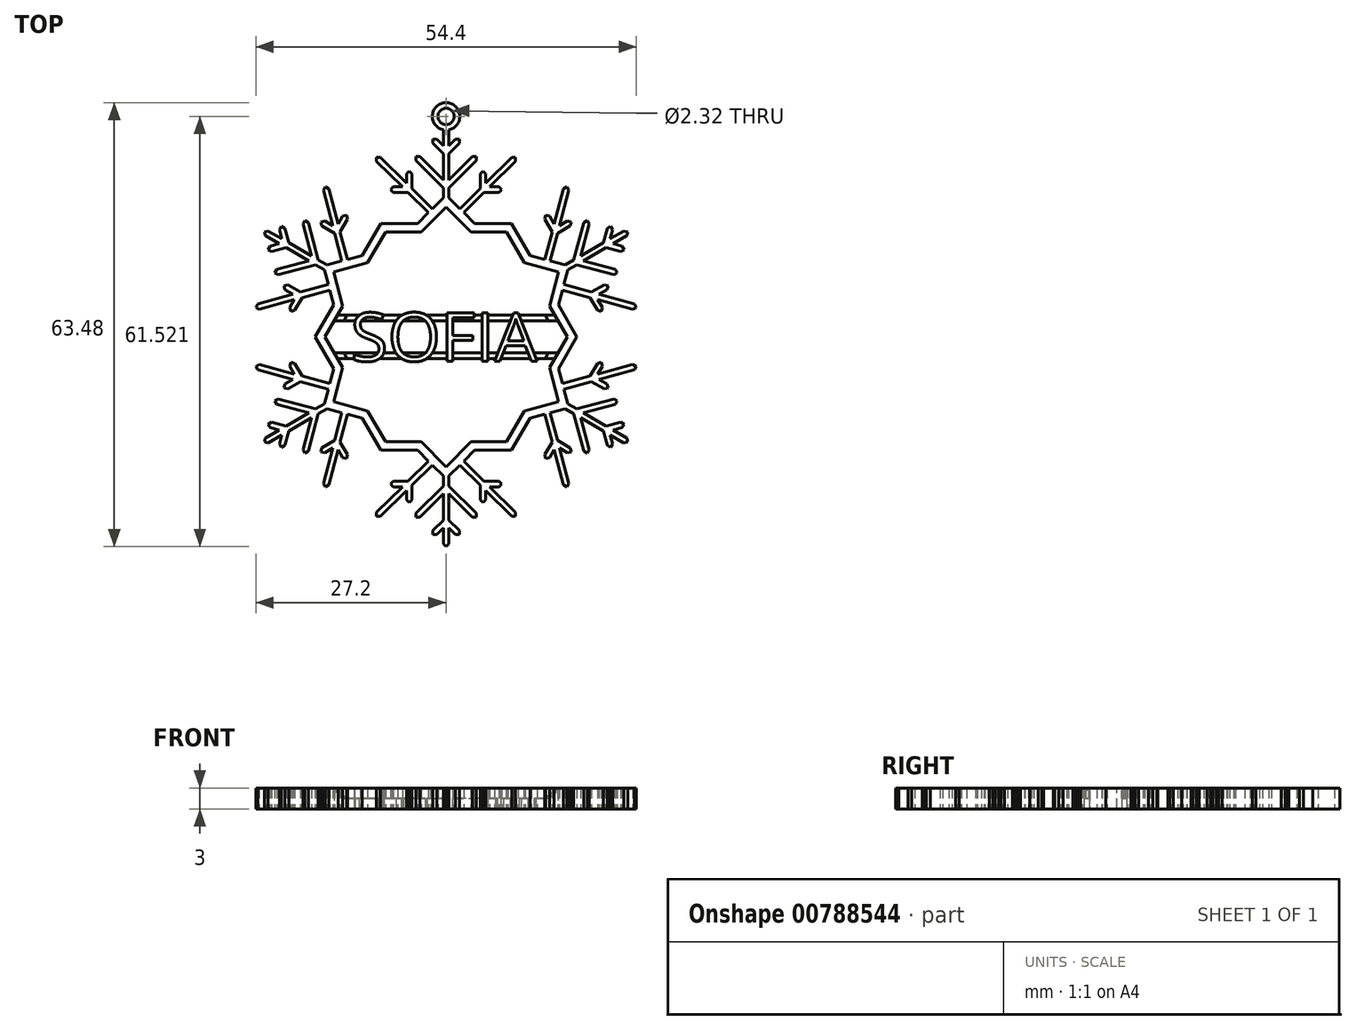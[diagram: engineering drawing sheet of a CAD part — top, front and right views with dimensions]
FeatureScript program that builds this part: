
annotation { "Feature Type Name" : "Feature", "Feature Type Description" : "" }
export const myFeature = defineFeature(function(context is Context, id is Id, definition is map)
    precondition{}
    {
        {
            var Q0;
            Q0=qCreatedBy(makeId("Top.planeOp"),FACE);
            var sketch = newSketch(context, id + "F0", { "sketchPlane" : qUnion([Q0])});
            skLineSegment(sketch, "E0", {"start": v(0, 0) * mm, "end": v(0, 68.59) * mm, "construction": true});
            skLineSegment(sketch, "E1", {"start": v(0, 0) * mm, "end": v(35, 60.61) * mm, "construction": true});
            skLineSegment(sketch, "E2", {"start": v(0, 0) * mm, "end": v(-32.87, 56.93) * mm, "construction": true});
            skLineSegment(sketch, "E3", {"start": v(-8.66, 15) * mm, "end": v(-3.57, 15) * mm});
            skLineSegment(sketch, "E4", {"start": v(-3.57, 15) * mm, "end": v(0, 18.57) * mm});
            skLineSegment(sketch, "E5", {"start": v(-0.4, 19.87) * mm, "end": v(-1.95, 18.32) * mm});
            skLineSegment(sketch, "E6", {"start": v(-4.07, 16.2) * mm, "end": v(-9.35, 16.2) * mm});
            skLineSegment(sketch, "E7", {"start": v(-0.4, 29.6) * mm, "end": v(0, 30) * mm});
            skLineSegment(sketch, "E8", {"start": v(-0.4, 27.32) * mm, "end": v(-1.35, 28.28) * mm});
            skLineSegment(sketch, "E9", {"start": v(-1.35, 28.28) * mm, "end": v(-1.92, 28.28) * mm});
            skLineSegment(sketch, "E10", {"start": v(-1.92, 28.28) * mm, "end": v(-1.92, 27.71) * mm});
            skLineSegment(sketch, "E11", {"start": v(-1.92, 27.71) * mm, "end": v(-0.4, 26.2) * mm});
            skLineSegment(sketch, "E12", {"start": v(-1.95, 18.32) * mm, "end": v(-4.86, 21.2) * mm});
            skLineSegment(sketch, "E13", {"start": v(-9.38, 25.67) * mm, "end": v(-9.94, 25.67) * mm});
            skLineSegment(sketch, "E14", {"start": v(-9.94, 25.67) * mm, "end": v(-9.94, 25.1) * mm});
            skLineSegment(sketch, "E15", {"start": v(-9.94, 25.1) * mm, "end": v(-6.24, 21.43) * mm});
            skLineSegment(sketch, "E16", {"start": v(-5.66, 22) * mm, "end": v(-5.66, 23.3) * mm});
            skLineSegment(sketch, "E17", {"start": v(-5.66, 23.3) * mm, "end": v(-5.27, 23.7) * mm});
            skLineSegment(sketch, "E18", {"start": v(-5.27, 23.7) * mm, "end": v(-4.86, 23.3) * mm});
            skLineSegment(sketch, "E19", {"start": v(-4.86, 23.3) * mm, "end": v(-4.86, 21.2) * mm});
            skLineSegment(sketch, "E20", {"start": v(-5.43, 20.63) * mm, "end": v(-7.54, 20.63) * mm});
            skLineSegment(sketch, "E21", {"start": v(-7.54, 20.63) * mm, "end": v(-7.94, 21.03) * mm});
            skLineSegment(sketch, "E22", {"start": v(-6.24, 21.43) * mm, "end": v(-7.54, 21.43) * mm});
            skLineSegment(sketch, "E23", {"start": v(-7.54, 21.43) * mm, "end": v(-7.94, 21.03) * mm});
            skLineSegment(sketch, "E24.trimOffspring", {"start": v(-2.52, 17.75) * mm, "end": v(-4.07, 16.2) * mm});
            skLineSegment(sketch, "E25", {"start": v(-0.4, 22.44) * mm, "end": v(-3.74, 25.77) * mm});
            skLineSegment(sketch, "E26", {"start": v(-3.74, 25.77) * mm, "end": v(-4.3, 25.77) * mm});
            skLineSegment(sketch, "E27", {"start": v(-4.3, 25.77) * mm, "end": v(-4.3, 25.2) * mm});
            skLineSegment(sketch, "E28", {"start": v(-4.3, 25.2) * mm, "end": v(-0.4, 21.3) * mm});
            skLineSegment(sketch, "E29.trimOffspring", {"start": v(-5.66, 22) * mm, "end": v(-9.38, 25.67) * mm});
            skLineSegment(sketch, "E30.trimOffspring", {"start": v(-5.43, 20.63) * mm, "end": v(-2.52, 17.75) * mm});
            skLineSegment(sketch, "E31.trimOffspring", {"start": v(-0.4, 22.44) * mm, "end": v(-0.4, 26.2) * mm});
            skLineSegment(sketch, "E32.trimOffspring", {"start": v(-0.4, 27.32) * mm, "end": v(-0.4, 29.6) * mm});
            skLineSegment(sketch, "E33", {"start": v(-0.4, 21.3) * mm, "end": v(-0.4, 19.87) * mm});
            skLineSegment(sketch, "E34.MirrorCS", {"start": v(0.4, 29.6) * mm, "end": v(0, 30) * mm});
            skLineSegment(sketch, "E35.MirrorCS", {"start": v(0.4, 27.32) * mm, "end": v(0.4, 29.6) * mm});
            skLineSegment(sketch, "E36.MirrorCS", {"start": v(0.4, 27.32) * mm, "end": v(1.35, 28.28) * mm});
            skLineSegment(sketch, "E37.MirrorCS", {"start": v(1.35, 28.28) * mm, "end": v(1.92, 28.28) * mm});
            skLineSegment(sketch, "E38.MirrorCS", {"start": v(1.92, 28.28) * mm, "end": v(1.92, 27.71) * mm});
            skLineSegment(sketch, "E39.MirrorCS", {"start": v(1.92, 27.71) * mm, "end": v(0.4, 26.2) * mm});
            skLineSegment(sketch, "E40.MirrorCS", {"start": v(0.4, 22.44) * mm, "end": v(0.4, 26.2) * mm});
            skLineSegment(sketch, "E41.MirrorCS", {"start": v(0.4, 22.44) * mm, "end": v(3.74, 25.77) * mm});
            skLineSegment(sketch, "E42.MirrorCS", {"start": v(3.74, 25.77) * mm, "end": v(4.3, 25.77) * mm});
            skLineSegment(sketch, "E43.MirrorCS", {"start": v(4.3, 25.77) * mm, "end": v(4.3, 25.2) * mm});
            skLineSegment(sketch, "E44.MirrorCS", {"start": v(4.3, 25.2) * mm, "end": v(0.4, 21.3) * mm});
            skLineSegment(sketch, "E45.MirrorCS", {"start": v(0.4, 21.3) * mm, "end": v(0.4, 19.87) * mm});
            skLineSegment(sketch, "E46.MirrorCS", {"start": v(0.4, 19.87) * mm, "end": v(1.95, 18.32) * mm});
            skLineSegment(sketch, "E47.MirrorCS", {"start": v(1.95, 18.32) * mm, "end": v(4.86, 21.2) * mm});
            skLineSegment(sketch, "E48.MirrorCS", {"start": v(4.86, 23.3) * mm, "end": v(4.86, 21.2) * mm});
            skLineSegment(sketch, "E49.MirrorCS", {"start": v(5.27, 23.7) * mm, "end": v(4.86, 23.3) * mm});
            skLineSegment(sketch, "E50.MirrorCS", {"start": v(5.66, 23.3) * mm, "end": v(5.27, 23.7) * mm});
            skLineSegment(sketch, "E51.MirrorCS", {"start": v(5.66, 22) * mm, "end": v(5.66, 23.3) * mm});
            skLineSegment(sketch, "E52.MirrorCS", {"start": v(5.66, 22) * mm, "end": v(9.38, 25.67) * mm});
            skLineSegment(sketch, "E53.MirrorCS", {"start": v(9.38, 25.67) * mm, "end": v(9.94, 25.67) * mm});
            skLineSegment(sketch, "E54.MirrorCS", {"start": v(9.94, 25.67) * mm, "end": v(9.94, 25.1) * mm});
            skLineSegment(sketch, "E55.MirrorCS", {"start": v(9.94, 25.1) * mm, "end": v(6.24, 21.43) * mm});
            skLineSegment(sketch, "E56.MirrorCS", {"start": v(6.24, 21.43) * mm, "end": v(7.54, 21.43) * mm});
            skLineSegment(sketch, "E57.MirrorCS", {"start": v(7.54, 21.43) * mm, "end": v(7.94, 21.03) * mm});
            skLineSegment(sketch, "E58.MirrorCS", {"start": v(7.54, 20.63) * mm, "end": v(7.94, 21.03) * mm});
            skLineSegment(sketch, "E59.MirrorCS", {"start": v(5.43, 20.63) * mm, "end": v(7.54, 20.63) * mm});
            skLineSegment(sketch, "E60.MirrorCS", {"start": v(5.43, 20.63) * mm, "end": v(2.52, 17.75) * mm});
            skLineSegment(sketch, "E61.MirrorCS", {"start": v(2.52, 17.75) * mm, "end": v(4.07, 16.2) * mm});
            skLineSegment(sketch, "E62.MirrorCS", {"start": v(4.07, 16.2) * mm, "end": v(9.35, 16.2) * mm});
            skLineSegment(sketch, "E63.MirrorCS", {"start": v(8.66, 15) * mm, "end": v(3.57, 15) * mm});
            skLineSegment(sketch, "E64.MirrorCS", {"start": v(3.57, 15) * mm, "end": v(0, 18.57) * mm});
            skLineSegment(sketch, "E65.1.0", {"start": v(-12, 11.62) * mm, "end": v(-9.35, 16.2) * mm});
            skLineSegment(sketch, "E65.1.1", {"start": v(-8.66, 15) * mm, "end": v(-11.2, 10.6) * mm});
            skLineSegment(sketch, "E65.1.2", {"start": v(-14.11, 11.06) * mm, "end": v(-12, 11.62) * mm});
            skLineSegment(sketch, "E65.1.3", {"start": v(-11.2, 10.6) * mm, "end": v(-16.08, 9.29) * mm});
            skLineSegment(sketch, "E65.1.4", {"start": v(-15.15, 15.02) * mm, "end": v(-14.11, 11.06) * mm});
            skLineSegment(sketch, "E65.1.5", {"start": v(-15.15, 15.02) * mm, "end": v(-14.1, 16.84) * mm});
            skLineSegment(sketch, "E65.1.6", {"start": v(-14.1, 16.84) * mm, "end": v(-14.25, 17.4) * mm});
            skLineSegment(sketch, "E65.1.7", {"start": v(-14.8, 17.25) * mm, "end": v(-14.25, 17.4) * mm});
            skLineSegment(sketch, "E65.1.8", {"start": v(-15.44, 16.12) * mm, "end": v(-14.8, 17.25) * mm});
            skLineSegment(sketch, "E65.1.9", {"start": v(-16.77, 21.16) * mm, "end": v(-15.44, 16.12) * mm});
            skLineSegment(sketch, "E65.1.10", {"start": v(-17.26, 21.44) * mm, "end": v(-16.77, 21.16) * mm});
            skLineSegment(sketch, "E65.1.11", {"start": v(-17.54, 20.95) * mm, "end": v(-17.26, 21.44) * mm});
            skLineSegment(sketch, "E65.1.12", {"start": v(-16.21, 15.9) * mm, "end": v(-17.54, 20.95) * mm});
            skLineSegment(sketch, "E65.1.13", {"start": v(-16.21, 15.9) * mm, "end": v(-17.35, 16.56) * mm});
            skLineSegment(sketch, "E65.1.14", {"start": v(-17.35, 16.56) * mm, "end": v(-17.9, 16.41) * mm});
            skLineSegment(sketch, "E65.1.15", {"start": v(-17.9, 16.41) * mm, "end": v(-17.75, 15.87) * mm});
            skLineSegment(sketch, "E65.1.16", {"start": v(-17.75, 15.87) * mm, "end": v(-15.93, 14.81) * mm});
            skLineSegment(sketch, "E65.1.17", {"start": v(-14.89, 10.85) * mm, "end": v(-15.93, 14.81) * mm});
            skLineSegment(sketch, "E65.1.18", {"start": v(-17, 10.28) * mm, "end": v(-14.89, 10.85) * mm});
            skLineSegment(sketch, "E65.1.19", {"start": v(-18.25, 11) * mm, "end": v(-17, 10.28) * mm});
            skLineSegment(sketch, "E65.1.20", {"start": v(-19.68, 16.33) * mm, "end": v(-18.25, 11) * mm});
            skLineSegment(sketch, "E65.1.21", {"start": v(-20.17, 16.61) * mm, "end": v(-19.68, 16.33) * mm});
            skLineSegment(sketch, "E65.1.22", {"start": v(-20.45, 16.13) * mm, "end": v(-20.17, 16.61) * mm});
            skLineSegment(sketch, "E65.1.23", {"start": v(-19.23, 11.56) * mm, "end": v(-20.45, 16.13) * mm});
            skLineSegment(sketch, "E65.1.24", {"start": v(-19.23, 11.56) * mm, "end": v(-22.48, 13.44) * mm});
            skLineSegment(sketch, "E65.1.25", {"start": v(-23.04, 15.52) * mm, "end": v(-22.48, 13.44) * mm});
            skLineSegment(sketch, "E65.1.26", {"start": v(-23.53, 15.8) * mm, "end": v(-23.04, 15.52) * mm});
            skLineSegment(sketch, "E65.1.27", {"start": v(-23.81, 15.31) * mm, "end": v(-23.53, 15.8) * mm});
            skLineSegment(sketch, "E65.1.28", {"start": v(-23.46, 14) * mm, "end": v(-23.81, 15.31) * mm});
            skLineSegment(sketch, "E65.1.29", {"start": v(-23.46, 14) * mm, "end": v(-25.43, 15.15) * mm});
            skLineSegment(sketch, "E65.1.30", {"start": v(-25.43, 15.15) * mm, "end": v(-25.98, 15) * mm});
            skLineSegment(sketch, "E65.1.31", {"start": v(-25.83, 14.45) * mm, "end": v(-25.98, 15) * mm});
            skLineSegment(sketch, "E65.1.32", {"start": v(-23.86, 13.32) * mm, "end": v(-25.83, 14.45) * mm});
            skLineSegment(sketch, "E65.1.33", {"start": v(-23.86, 13.32) * mm, "end": v(-25.16, 12.97) * mm});
            skLineSegment(sketch, "E65.1.34", {"start": v(-25.16, 12.97) * mm, "end": v(-25.45, 12.48) * mm});
            skLineSegment(sketch, "E65.1.35", {"start": v(-25.45, 12.48) * mm, "end": v(-24.96, 12.2) * mm});
            skLineSegment(sketch, "E65.1.36", {"start": v(-24.96, 12.2) * mm, "end": v(-22.88, 12.75) * mm});
            skLineSegment(sketch, "E65.1.37", {"start": v(-19.63, 10.87) * mm, "end": v(-22.88, 12.75) * mm});
            skLineSegment(sketch, "E65.1.38", {"start": v(-19.63, 10.87) * mm, "end": v(-24.2, 9.65) * mm});
            skLineSegment(sketch, "E65.1.39", {"start": v(-24.2, 9.65) * mm, "end": v(-24.47, 9.16) * mm});
            skLineSegment(sketch, "E65.1.40", {"start": v(-24.47, 9.16) * mm, "end": v(-23.98, 8.88) * mm});
            skLineSegment(sketch, "E65.1.41", {"start": v(-23.98, 8.88) * mm, "end": v(-18.65, 10.3) * mm});
            skLineSegment(sketch, "E65.1.42", {"start": v(-18.65, 10.3) * mm, "end": v(-17.4, 9.59) * mm});
            skLineSegment(sketch, "E65.1.43", {"start": v(-17.4, 9.59) * mm, "end": v(-16.84, 7.47) * mm});
            skLineSegment(sketch, "E65.1.44", {"start": v(-16.84, 7.47) * mm, "end": v(-20.8, 6.39) * mm});
            skLineSegment(sketch, "E65.1.45", {"start": v(-22.62, 7.44) * mm, "end": v(-20.8, 6.39) * mm});
            skLineSegment(sketch, "E65.1.46", {"start": v(-23.16, 7.3) * mm, "end": v(-22.62, 7.44) * mm});
            skLineSegment(sketch, "E65.1.47", {"start": v(-23.01, 6.74) * mm, "end": v(-23.16, 7.3) * mm});
            skLineSegment(sketch, "E65.1.48", {"start": v(-21.88, 6.09) * mm, "end": v(-23.01, 6.74) * mm});
            skLineSegment(sketch, "E65.1.49", {"start": v(-21.88, 6.09) * mm, "end": v(-26.92, 4.71) * mm});
            skLineSegment(sketch, "E65.1.50", {"start": v(-26.92, 4.71) * mm, "end": v(-27.2, 4.22) * mm});
            skLineSegment(sketch, "E65.1.51", {"start": v(-27.2, 4.22) * mm, "end": v(-26.7, 3.94) * mm});
            skLineSegment(sketch, "E65.1.52", {"start": v(-26.7, 3.94) * mm, "end": v(-21.68, 5.31) * mm});
            skLineSegment(sketch, "E65.1.53", {"start": v(-21.68, 5.31) * mm, "end": v(-22.33, 4.19) * mm});
            skLineSegment(sketch, "E65.1.54", {"start": v(-22.33, 4.19) * mm, "end": v(-22.18, 3.64) * mm});
            skLineSegment(sketch, "E65.1.55", {"start": v(-21.64, 3.8) * mm, "end": v(-22.18, 3.64) * mm});
            skLineSegment(sketch, "E65.1.56", {"start": v(-20.59, 5.61) * mm, "end": v(-21.64, 3.8) * mm});
            skLineSegment(sketch, "E65.1.57", {"start": v(-20.59, 5.61) * mm, "end": v(-16.63, 6.7) * mm});
            skLineSegment(sketch, "E65.1.58", {"start": v(-16.63, 6.7) * mm, "end": v(-16.06, 4.58) * mm});
            skLineSegment(sketch, "E65.1.59", {"start": v(-16.06, 4.58) * mm, "end": v(-18.7, 0) * mm});
            skLineSegment(sketch, "E65.1.60", {"start": v(-17.32, 0) * mm, "end": v(-14.78, 4.4) * mm});
            skLineSegment(sketch, "E65.1.61", {"start": v(-14.78, 4.4) * mm, "end": v(-16.08, 9.29) * mm});
            skLineSegment(sketch, "E65.2.0", {"start": v(-16.06, -4.58) * mm, "end": v(-18.7, 0) * mm});
            skLineSegment(sketch, "E65.2.1", {"start": v(-17.32, 0) * mm, "end": v(-14.78, -4.4) * mm});
            skLineSegment(sketch, "E65.2.2", {"start": v(-16.63, -6.7) * mm, "end": v(-16.06, -4.58) * mm});
            skLineSegment(sketch, "E65.2.3", {"start": v(-14.78, -4.4) * mm, "end": v(-16.08, -9.29) * mm});
            skLineSegment(sketch, "E65.2.4", {"start": v(-20.59, -5.61) * mm, "end": v(-16.63, -6.7) * mm});
            skLineSegment(sketch, "E65.2.5", {"start": v(-20.59, -5.61) * mm, "end": v(-21.64, -3.8) * mm});
            skLineSegment(sketch, "E65.2.6", {"start": v(-21.64, -3.8) * mm, "end": v(-22.18, -3.64) * mm});
            skLineSegment(sketch, "E65.2.7", {"start": v(-22.33, -4.19) * mm, "end": v(-22.18, -3.64) * mm});
            skLineSegment(sketch, "E65.2.8", {"start": v(-21.68, -5.31) * mm, "end": v(-22.33, -4.19) * mm});
            skLineSegment(sketch, "E65.2.9", {"start": v(-26.7, -3.94) * mm, "end": v(-21.68, -5.31) * mm});
            skLineSegment(sketch, "E65.2.10", {"start": v(-27.2, -4.22) * mm, "end": v(-26.7, -3.94) * mm});
            skLineSegment(sketch, "E65.2.11", {"start": v(-26.92, -4.71) * mm, "end": v(-27.2, -4.22) * mm});
            skLineSegment(sketch, "E65.2.12", {"start": v(-21.88, -6.09) * mm, "end": v(-26.92, -4.71) * mm});
            skLineSegment(sketch, "E65.2.13", {"start": v(-21.88, -6.09) * mm, "end": v(-23.01, -6.74) * mm});
            skLineSegment(sketch, "E65.2.14", {"start": v(-23.01, -6.74) * mm, "end": v(-23.16, -7.3) * mm});
            skLineSegment(sketch, "E65.2.15", {"start": v(-23.16, -7.3) * mm, "end": v(-22.62, -7.44) * mm});
            skLineSegment(sketch, "E65.2.16", {"start": v(-22.62, -7.44) * mm, "end": v(-20.8, -6.39) * mm});
            skLineSegment(sketch, "E65.2.17", {"start": v(-16.84, -7.47) * mm, "end": v(-20.8, -6.39) * mm});
            skLineSegment(sketch, "E65.2.18", {"start": v(-17.4, -9.59) * mm, "end": v(-16.84, -7.47) * mm});
            skLineSegment(sketch, "E65.2.19", {"start": v(-18.65, -10.3) * mm, "end": v(-17.4, -9.59) * mm});
            skLineSegment(sketch, "E65.2.20", {"start": v(-23.98, -8.88) * mm, "end": v(-18.65, -10.3) * mm});
            skLineSegment(sketch, "E65.2.21", {"start": v(-24.47, -9.16) * mm, "end": v(-23.98, -8.88) * mm});
            skLineSegment(sketch, "E65.2.22", {"start": v(-24.2, -9.65) * mm, "end": v(-24.47, -9.16) * mm});
            skLineSegment(sketch, "E65.2.23", {"start": v(-19.63, -10.87) * mm, "end": v(-24.2, -9.65) * mm});
            skLineSegment(sketch, "E65.2.24", {"start": v(-19.63, -10.87) * mm, "end": v(-22.88, -12.75) * mm});
            skLineSegment(sketch, "E65.2.25", {"start": v(-24.96, -12.2) * mm, "end": v(-22.88, -12.75) * mm});
            skLineSegment(sketch, "E65.2.26", {"start": v(-25.45, -12.48) * mm, "end": v(-24.96, -12.2) * mm});
            skLineSegment(sketch, "E65.2.27", {"start": v(-25.16, -12.97) * mm, "end": v(-25.45, -12.48) * mm});
            skLineSegment(sketch, "E65.2.28", {"start": v(-23.86, -13.32) * mm, "end": v(-25.16, -12.97) * mm});
            skLineSegment(sketch, "E65.2.29", {"start": v(-23.86, -13.32) * mm, "end": v(-25.83, -14.45) * mm});
            skLineSegment(sketch, "E65.2.30", {"start": v(-25.83, -14.45) * mm, "end": v(-25.98, -15) * mm});
            skLineSegment(sketch, "E65.2.31", {"start": v(-25.43, -15.15) * mm, "end": v(-25.98, -15) * mm});
            skLineSegment(sketch, "E65.2.32", {"start": v(-23.46, -14) * mm, "end": v(-25.43, -15.15) * mm});
            skLineSegment(sketch, "E65.2.33", {"start": v(-23.46, -14) * mm, "end": v(-23.81, -15.31) * mm});
            skLineSegment(sketch, "E65.2.34", {"start": v(-23.81, -15.31) * mm, "end": v(-23.53, -15.8) * mm});
            skLineSegment(sketch, "E65.2.35", {"start": v(-23.53, -15.8) * mm, "end": v(-23.04, -15.52) * mm});
            skLineSegment(sketch, "E65.2.36", {"start": v(-23.04, -15.52) * mm, "end": v(-22.48, -13.44) * mm});
            skLineSegment(sketch, "E65.2.37", {"start": v(-19.23, -11.56) * mm, "end": v(-22.48, -13.44) * mm});
            skLineSegment(sketch, "E65.2.38", {"start": v(-19.23, -11.56) * mm, "end": v(-20.45, -16.13) * mm});
            skLineSegment(sketch, "E65.2.39", {"start": v(-20.45, -16.13) * mm, "end": v(-20.17, -16.61) * mm});
            skLineSegment(sketch, "E65.2.40", {"start": v(-20.17, -16.61) * mm, "end": v(-19.68, -16.33) * mm});
            skLineSegment(sketch, "E65.2.41", {"start": v(-19.68, -16.33) * mm, "end": v(-18.25, -11) * mm});
            skLineSegment(sketch, "E65.2.42", {"start": v(-18.25, -11) * mm, "end": v(-17, -10.28) * mm});
            skLineSegment(sketch, "E65.2.43", {"start": v(-17, -10.28) * mm, "end": v(-14.89, -10.85) * mm});
            skLineSegment(sketch, "E65.2.44", {"start": v(-14.89, -10.85) * mm, "end": v(-15.93, -14.81) * mm});
            skLineSegment(sketch, "E65.2.45", {"start": v(-17.75, -15.87) * mm, "end": v(-15.93, -14.81) * mm});
            skLineSegment(sketch, "E65.2.46", {"start": v(-17.9, -16.41) * mm, "end": v(-17.75, -15.87) * mm});
            skLineSegment(sketch, "E65.2.47", {"start": v(-17.35, -16.56) * mm, "end": v(-17.9, -16.41) * mm});
            skLineSegment(sketch, "E65.2.48", {"start": v(-16.21, -15.9) * mm, "end": v(-17.35, -16.56) * mm});
            skLineSegment(sketch, "E65.2.49", {"start": v(-16.21, -15.9) * mm, "end": v(-17.54, -20.95) * mm});
            skLineSegment(sketch, "E65.2.50", {"start": v(-17.54, -20.95) * mm, "end": v(-17.26, -21.44) * mm});
            skLineSegment(sketch, "E65.2.51", {"start": v(-17.26, -21.44) * mm, "end": v(-16.77, -21.16) * mm});
            skLineSegment(sketch, "E65.2.52", {"start": v(-16.77, -21.16) * mm, "end": v(-15.44, -16.12) * mm});
            skLineSegment(sketch, "E65.2.53", {"start": v(-15.44, -16.12) * mm, "end": v(-14.8, -17.25) * mm});
            skLineSegment(sketch, "E65.2.54", {"start": v(-14.8, -17.25) * mm, "end": v(-14.25, -17.4) * mm});
            skLineSegment(sketch, "E65.2.55", {"start": v(-14.1, -16.84) * mm, "end": v(-14.25, -17.4) * mm});
            skLineSegment(sketch, "E65.2.56", {"start": v(-15.15, -15.02) * mm, "end": v(-14.1, -16.84) * mm});
            skLineSegment(sketch, "E65.2.57", {"start": v(-15.15, -15.02) * mm, "end": v(-14.11, -11.06) * mm});
            skLineSegment(sketch, "E65.2.58", {"start": v(-14.11, -11.06) * mm, "end": v(-12, -11.62) * mm});
            skLineSegment(sketch, "E65.2.59", {"start": v(-12, -11.62) * mm, "end": v(-9.35, -16.2) * mm});
            skLineSegment(sketch, "E65.2.60", {"start": v(-8.66, -15) * mm, "end": v(-11.2, -10.6) * mm});
            skLineSegment(sketch, "E65.2.61", {"start": v(-11.2, -10.6) * mm, "end": v(-16.08, -9.29) * mm});
            skLineSegment(sketch, "E65.3.0", {"start": v(-4.07, -16.2) * mm, "end": v(-9.35, -16.2) * mm});
            skLineSegment(sketch, "E65.3.1", {"start": v(-8.66, -15) * mm, "end": v(-3.57, -15) * mm});
            skLineSegment(sketch, "E65.3.2", {"start": v(-2.52, -17.75) * mm, "end": v(-4.07, -16.2) * mm});
            skLineSegment(sketch, "E65.3.3", {"start": v(-3.57, -15) * mm, "end": v(0, -18.57) * mm});
            skLineSegment(sketch, "E65.3.4", {"start": v(-5.43, -20.63) * mm, "end": v(-2.52, -17.75) * mm});
            skLineSegment(sketch, "E65.3.5", {"start": v(-5.43, -20.63) * mm, "end": v(-7.54, -20.63) * mm});
            skLineSegment(sketch, "E65.3.6", {"start": v(-7.54, -20.63) * mm, "end": v(-7.94, -21.03) * mm});
            skLineSegment(sketch, "E65.3.7", {"start": v(-7.54, -21.43) * mm, "end": v(-7.94, -21.03) * mm});
            skLineSegment(sketch, "E65.3.8", {"start": v(-6.24, -21.43) * mm, "end": v(-7.54, -21.43) * mm});
            skLineSegment(sketch, "E65.3.9", {"start": v(-9.94, -25.1) * mm, "end": v(-6.24, -21.43) * mm});
            skLineSegment(sketch, "E65.3.10", {"start": v(-9.94, -25.67) * mm, "end": v(-9.94, -25.1) * mm});
            skLineSegment(sketch, "E65.3.11", {"start": v(-9.38, -25.67) * mm, "end": v(-9.94, -25.67) * mm});
            skLineSegment(sketch, "E65.3.12", {"start": v(-5.66, -22) * mm, "end": v(-9.38, -25.67) * mm});
            skLineSegment(sketch, "E65.3.13", {"start": v(-5.66, -22) * mm, "end": v(-5.66, -23.3) * mm});
            skLineSegment(sketch, "E65.3.14", {"start": v(-5.66, -23.3) * mm, "end": v(-5.27, -23.7) * mm});
            skLineSegment(sketch, "E65.3.15", {"start": v(-5.27, -23.7) * mm, "end": v(-4.86, -23.3) * mm});
            skLineSegment(sketch, "E65.3.16", {"start": v(-4.86, -23.3) * mm, "end": v(-4.86, -21.2) * mm});
            skLineSegment(sketch, "E65.3.17", {"start": v(-1.95, -18.32) * mm, "end": v(-4.86, -21.2) * mm});
            skLineSegment(sketch, "E65.3.18", {"start": v(-0.4, -19.87) * mm, "end": v(-1.95, -18.32) * mm});
            skLineSegment(sketch, "E65.3.19", {"start": v(-0.4, -21.3) * mm, "end": v(-0.4, -19.87) * mm});
            skLineSegment(sketch, "E65.3.20", {"start": v(-4.3, -25.2) * mm, "end": v(-0.4, -21.3) * mm});
            skLineSegment(sketch, "E65.3.21", {"start": v(-4.3, -25.77) * mm, "end": v(-4.3, -25.2) * mm});
            skLineSegment(sketch, "E65.3.22", {"start": v(-3.74, -25.77) * mm, "end": v(-4.3, -25.77) * mm});
            skLineSegment(sketch, "E65.3.23", {"start": v(-0.4, -22.44) * mm, "end": v(-3.74, -25.77) * mm});
            skLineSegment(sketch, "E65.3.24", {"start": v(-0.4, -22.44) * mm, "end": v(-0.4, -26.2) * mm});
            skLineSegment(sketch, "E65.3.25", {"start": v(-1.92, -27.71) * mm, "end": v(-0.4, -26.2) * mm});
            skLineSegment(sketch, "E65.3.26", {"start": v(-1.92, -28.28) * mm, "end": v(-1.92, -27.71) * mm});
            skLineSegment(sketch, "E65.3.27", {"start": v(-1.35, -28.28) * mm, "end": v(-1.92, -28.28) * mm});
            skLineSegment(sketch, "E65.3.28", {"start": v(-0.4, -27.32) * mm, "end": v(-1.35, -28.28) * mm});
            skLineSegment(sketch, "E65.3.29", {"start": v(-0.4, -27.32) * mm, "end": v(-0.4, -29.6) * mm});
            skLineSegment(sketch, "E65.3.30", {"start": v(-0.4, -29.6) * mm, "end": v(0, -30) * mm});
            skLineSegment(sketch, "E65.3.31", {"start": v(0.4, -29.6) * mm, "end": v(0, -30) * mm});
            skLineSegment(sketch, "E65.3.32", {"start": v(0.4, -27.32) * mm, "end": v(0.4, -29.6) * mm});
            skLineSegment(sketch, "E65.3.33", {"start": v(0.4, -27.32) * mm, "end": v(1.35, -28.28) * mm});
            skLineSegment(sketch, "E65.3.34", {"start": v(1.35, -28.28) * mm, "end": v(1.92, -28.28) * mm});
            skLineSegment(sketch, "E65.3.35", {"start": v(1.92, -28.28) * mm, "end": v(1.92, -27.71) * mm});
            skLineSegment(sketch, "E65.3.36", {"start": v(1.92, -27.71) * mm, "end": v(0.4, -26.2) * mm});
            skLineSegment(sketch, "E65.3.37", {"start": v(0.4, -22.44) * mm, "end": v(0.4, -26.2) * mm});
            skLineSegment(sketch, "E65.3.38", {"start": v(0.4, -22.44) * mm, "end": v(3.74, -25.77) * mm});
            skLineSegment(sketch, "E65.3.39", {"start": v(3.74, -25.77) * mm, "end": v(4.3, -25.77) * mm});
            skLineSegment(sketch, "E65.3.40", {"start": v(4.3, -25.77) * mm, "end": v(4.3, -25.2) * mm});
            skLineSegment(sketch, "E65.3.41", {"start": v(4.3, -25.2) * mm, "end": v(0.4, -21.3) * mm});
            skLineSegment(sketch, "E65.3.42", {"start": v(0.4, -21.3) * mm, "end": v(0.4, -19.87) * mm});
            skLineSegment(sketch, "E65.3.43", {"start": v(0.4, -19.87) * mm, "end": v(1.95, -18.32) * mm});
            skLineSegment(sketch, "E65.3.44", {"start": v(1.95, -18.32) * mm, "end": v(4.86, -21.2) * mm});
            skLineSegment(sketch, "E65.3.45", {"start": v(4.86, -23.3) * mm, "end": v(4.86, -21.2) * mm});
            skLineSegment(sketch, "E65.3.46", {"start": v(5.27, -23.7) * mm, "end": v(4.86, -23.3) * mm});
            skLineSegment(sketch, "E65.3.47", {"start": v(5.66, -23.3) * mm, "end": v(5.27, -23.7) * mm});
            skLineSegment(sketch, "E65.3.48", {"start": v(5.66, -22) * mm, "end": v(5.66, -23.3) * mm});
            skLineSegment(sketch, "E65.3.49", {"start": v(5.66, -22) * mm, "end": v(9.38, -25.67) * mm});
            skLineSegment(sketch, "E65.3.50", {"start": v(9.38, -25.67) * mm, "end": v(9.94, -25.67) * mm});
            skLineSegment(sketch, "E65.3.51", {"start": v(9.94, -25.67) * mm, "end": v(9.94, -25.1) * mm});
            skLineSegment(sketch, "E65.3.52", {"start": v(9.94, -25.1) * mm, "end": v(6.24, -21.43) * mm});
            skLineSegment(sketch, "E65.3.53", {"start": v(6.24, -21.43) * mm, "end": v(7.54, -21.43) * mm});
            skLineSegment(sketch, "E65.3.54", {"start": v(7.54, -21.43) * mm, "end": v(7.94, -21.03) * mm});
            skLineSegment(sketch, "E65.3.55", {"start": v(7.54, -20.63) * mm, "end": v(7.94, -21.03) * mm});
            skLineSegment(sketch, "E65.3.56", {"start": v(5.43, -20.63) * mm, "end": v(7.54, -20.63) * mm});
            skLineSegment(sketch, "E65.3.57", {"start": v(5.43, -20.63) * mm, "end": v(2.52, -17.75) * mm});
            skLineSegment(sketch, "E65.3.58", {"start": v(2.52, -17.75) * mm, "end": v(4.07, -16.2) * mm});
            skLineSegment(sketch, "E65.3.59", {"start": v(4.07, -16.2) * mm, "end": v(9.35, -16.2) * mm});
            skLineSegment(sketch, "E65.3.60", {"start": v(8.66, -15) * mm, "end": v(3.57, -15) * mm});
            skLineSegment(sketch, "E65.3.61", {"start": v(3.57, -15) * mm, "end": v(0, -18.57) * mm});
            skLineSegment(sketch, "E65.4.0", {"start": v(12, -11.62) * mm, "end": v(9.35, -16.2) * mm});
            skLineSegment(sketch, "E65.4.1", {"start": v(8.66, -15) * mm, "end": v(11.2, -10.6) * mm});
            skLineSegment(sketch, "E65.4.2", {"start": v(14.11, -11.06) * mm, "end": v(12, -11.62) * mm});
            skLineSegment(sketch, "E65.4.3", {"start": v(11.2, -10.6) * mm, "end": v(16.08, -9.29) * mm});
            skLineSegment(sketch, "E65.4.4", {"start": v(15.15, -15.02) * mm, "end": v(14.11, -11.06) * mm});
            skLineSegment(sketch, "E65.4.5", {"start": v(15.15, -15.02) * mm, "end": v(14.1, -16.84) * mm});
            skLineSegment(sketch, "E65.4.6", {"start": v(14.1, -16.84) * mm, "end": v(14.25, -17.4) * mm});
            skLineSegment(sketch, "E65.4.7", {"start": v(14.8, -17.25) * mm, "end": v(14.25, -17.4) * mm});
            skLineSegment(sketch, "E65.4.8", {"start": v(15.44, -16.12) * mm, "end": v(14.8, -17.25) * mm});
            skLineSegment(sketch, "E65.4.9", {"start": v(16.77, -21.16) * mm, "end": v(15.44, -16.12) * mm});
            skLineSegment(sketch, "E65.4.10", {"start": v(17.26, -21.44) * mm, "end": v(16.77, -21.16) * mm});
            skLineSegment(sketch, "E65.4.11", {"start": v(17.54, -20.95) * mm, "end": v(17.26, -21.44) * mm});
            skLineSegment(sketch, "E65.4.12", {"start": v(16.21, -15.9) * mm, "end": v(17.54, -20.95) * mm});
            skLineSegment(sketch, "E65.4.13", {"start": v(16.21, -15.9) * mm, "end": v(17.35, -16.56) * mm});
            skLineSegment(sketch, "E65.4.14", {"start": v(17.35, -16.56) * mm, "end": v(17.9, -16.41) * mm});
            skLineSegment(sketch, "E65.4.15", {"start": v(17.9, -16.41) * mm, "end": v(17.75, -15.87) * mm});
            skLineSegment(sketch, "E65.4.16", {"start": v(17.75, -15.87) * mm, "end": v(15.93, -14.81) * mm});
            skLineSegment(sketch, "E65.4.17", {"start": v(14.89, -10.85) * mm, "end": v(15.93, -14.81) * mm});
            skLineSegment(sketch, "E65.4.18", {"start": v(17, -10.28) * mm, "end": v(14.89, -10.85) * mm});
            skLineSegment(sketch, "E65.4.19", {"start": v(18.25, -11) * mm, "end": v(17, -10.28) * mm});
            skLineSegment(sketch, "E65.4.20", {"start": v(19.68, -16.33) * mm, "end": v(18.25, -11) * mm});
            skLineSegment(sketch, "E65.4.21", {"start": v(20.17, -16.61) * mm, "end": v(19.68, -16.33) * mm});
            skLineSegment(sketch, "E65.4.22", {"start": v(20.45, -16.13) * mm, "end": v(20.17, -16.61) * mm});
            skLineSegment(sketch, "E65.4.23", {"start": v(19.23, -11.56) * mm, "end": v(20.45, -16.13) * mm});
            skLineSegment(sketch, "E65.4.24", {"start": v(19.23, -11.56) * mm, "end": v(22.48, -13.44) * mm});
            skLineSegment(sketch, "E65.4.25", {"start": v(23.04, -15.52) * mm, "end": v(22.48, -13.44) * mm});
            skLineSegment(sketch, "E65.4.26", {"start": v(23.53, -15.8) * mm, "end": v(23.04, -15.52) * mm});
            skLineSegment(sketch, "E65.4.27", {"start": v(23.81, -15.31) * mm, "end": v(23.53, -15.8) * mm});
            skLineSegment(sketch, "E65.4.28", {"start": v(23.46, -14) * mm, "end": v(23.81, -15.31) * mm});
            skLineSegment(sketch, "E65.4.29", {"start": v(23.46, -14) * mm, "end": v(25.43, -15.15) * mm});
            skLineSegment(sketch, "E65.4.30", {"start": v(25.43, -15.15) * mm, "end": v(25.98, -15) * mm});
            skLineSegment(sketch, "E65.4.31", {"start": v(25.83, -14.45) * mm, "end": v(25.98, -15) * mm});
            skLineSegment(sketch, "E65.4.32", {"start": v(23.86, -13.32) * mm, "end": v(25.83, -14.45) * mm});
            skLineSegment(sketch, "E65.4.33", {"start": v(23.86, -13.32) * mm, "end": v(25.16, -12.97) * mm});
            skLineSegment(sketch, "E65.4.34", {"start": v(25.16, -12.97) * mm, "end": v(25.45, -12.48) * mm});
            skLineSegment(sketch, "E65.4.35", {"start": v(25.45, -12.48) * mm, "end": v(24.96, -12.2) * mm});
            skLineSegment(sketch, "E65.4.36", {"start": v(24.96, -12.2) * mm, "end": v(22.88, -12.75) * mm});
            skLineSegment(sketch, "E65.4.37", {"start": v(19.63, -10.87) * mm, "end": v(22.88, -12.75) * mm});
            skLineSegment(sketch, "E65.4.38", {"start": v(19.63, -10.87) * mm, "end": v(24.2, -9.65) * mm});
            skLineSegment(sketch, "E65.4.39", {"start": v(24.2, -9.65) * mm, "end": v(24.47, -9.16) * mm});
            skLineSegment(sketch, "E65.4.40", {"start": v(24.47, -9.16) * mm, "end": v(23.98, -8.88) * mm});
            skLineSegment(sketch, "E65.4.41", {"start": v(23.98, -8.88) * mm, "end": v(18.65, -10.3) * mm});
            skLineSegment(sketch, "E65.4.42", {"start": v(18.65, -10.3) * mm, "end": v(17.4, -9.59) * mm});
            skLineSegment(sketch, "E65.4.43", {"start": v(17.4, -9.59) * mm, "end": v(16.84, -7.47) * mm});
            skLineSegment(sketch, "E65.4.44", {"start": v(16.84, -7.47) * mm, "end": v(20.8, -6.39) * mm});
            skLineSegment(sketch, "E65.4.45", {"start": v(22.62, -7.44) * mm, "end": v(20.8, -6.39) * mm});
            skLineSegment(sketch, "E65.4.46", {"start": v(23.16, -7.3) * mm, "end": v(22.62, -7.44) * mm});
            skLineSegment(sketch, "E65.4.47", {"start": v(23.01, -6.74) * mm, "end": v(23.16, -7.3) * mm});
            skLineSegment(sketch, "E65.4.48", {"start": v(21.88, -6.09) * mm, "end": v(23.01, -6.74) * mm});
            skLineSegment(sketch, "E65.4.49", {"start": v(21.88, -6.09) * mm, "end": v(26.92, -4.71) * mm});
            skLineSegment(sketch, "E65.4.50", {"start": v(26.92, -4.71) * mm, "end": v(27.2, -4.22) * mm});
            skLineSegment(sketch, "E65.4.51", {"start": v(27.2, -4.22) * mm, "end": v(26.7, -3.94) * mm});
            skLineSegment(sketch, "E65.4.52", {"start": v(26.7, -3.94) * mm, "end": v(21.68, -5.31) * mm});
            skLineSegment(sketch, "E65.4.53", {"start": v(21.68, -5.31) * mm, "end": v(22.33, -4.19) * mm});
            skLineSegment(sketch, "E65.4.54", {"start": v(22.33, -4.19) * mm, "end": v(22.18, -3.64) * mm});
            skLineSegment(sketch, "E65.4.55", {"start": v(21.64, -3.8) * mm, "end": v(22.18, -3.64) * mm});
            skLineSegment(sketch, "E65.4.56", {"start": v(20.59, -5.61) * mm, "end": v(21.64, -3.8) * mm});
            skLineSegment(sketch, "E65.4.57", {"start": v(20.59, -5.61) * mm, "end": v(16.63, -6.7) * mm});
            skLineSegment(sketch, "E65.4.58", {"start": v(16.63, -6.7) * mm, "end": v(16.06, -4.58) * mm});
            skLineSegment(sketch, "E65.4.59", {"start": v(16.06, -4.58) * mm, "end": v(18.7, 0) * mm});
            skLineSegment(sketch, "E65.4.60", {"start": v(17.32, 0) * mm, "end": v(14.78, -4.4) * mm});
            skLineSegment(sketch, "E65.4.61", {"start": v(14.78, -4.4) * mm, "end": v(16.08, -9.29) * mm});
            skLineSegment(sketch, "E65.5.0", {"start": v(16.06, 4.58) * mm, "end": v(18.7, 0) * mm});
            skLineSegment(sketch, "E65.5.1", {"start": v(17.32, 0) * mm, "end": v(14.78, 4.4) * mm});
            skLineSegment(sketch, "E65.5.2", {"start": v(16.63, 6.7) * mm, "end": v(16.06, 4.58) * mm});
            skLineSegment(sketch, "E65.5.3", {"start": v(14.78, 4.4) * mm, "end": v(16.08, 9.29) * mm});
            skLineSegment(sketch, "E65.5.4", {"start": v(20.59, 5.61) * mm, "end": v(16.63, 6.7) * mm});
            skLineSegment(sketch, "E65.5.5", {"start": v(20.59, 5.61) * mm, "end": v(21.64, 3.8) * mm});
            skLineSegment(sketch, "E65.5.6", {"start": v(21.64, 3.8) * mm, "end": v(22.18, 3.64) * mm});
            skLineSegment(sketch, "E65.5.7", {"start": v(22.33, 4.19) * mm, "end": v(22.18, 3.64) * mm});
            skLineSegment(sketch, "E65.5.8", {"start": v(21.68, 5.31) * mm, "end": v(22.33, 4.19) * mm});
            skLineSegment(sketch, "E65.5.9", {"start": v(26.7, 3.94) * mm, "end": v(21.68, 5.31) * mm});
            skLineSegment(sketch, "E65.5.10", {"start": v(27.2, 4.22) * mm, "end": v(26.7, 3.94) * mm});
            skLineSegment(sketch, "E65.5.11", {"start": v(26.92, 4.71) * mm, "end": v(27.2, 4.22) * mm});
            skLineSegment(sketch, "E65.5.12", {"start": v(21.88, 6.09) * mm, "end": v(26.92, 4.71) * mm});
            skLineSegment(sketch, "E65.5.13", {"start": v(21.88, 6.09) * mm, "end": v(23.01, 6.74) * mm});
            skLineSegment(sketch, "E65.5.14", {"start": v(23.01, 6.74) * mm, "end": v(23.16, 7.3) * mm});
            skLineSegment(sketch, "E65.5.15", {"start": v(23.16, 7.3) * mm, "end": v(22.62, 7.44) * mm});
            skLineSegment(sketch, "E65.5.16", {"start": v(22.62, 7.44) * mm, "end": v(20.8, 6.39) * mm});
            skLineSegment(sketch, "E65.5.17", {"start": v(16.84, 7.47) * mm, "end": v(20.8, 6.39) * mm});
            skLineSegment(sketch, "E65.5.18", {"start": v(17.4, 9.59) * mm, "end": v(16.84, 7.47) * mm});
            skLineSegment(sketch, "E65.5.19", {"start": v(18.65, 10.3) * mm, "end": v(17.4, 9.59) * mm});
            skLineSegment(sketch, "E65.5.20", {"start": v(23.98, 8.88) * mm, "end": v(18.65, 10.3) * mm});
            skLineSegment(sketch, "E65.5.21", {"start": v(24.47, 9.16) * mm, "end": v(23.98, 8.88) * mm});
            skLineSegment(sketch, "E65.5.22", {"start": v(24.2, 9.65) * mm, "end": v(24.47, 9.16) * mm});
            skLineSegment(sketch, "E65.5.23", {"start": v(19.63, 10.87) * mm, "end": v(24.2, 9.65) * mm});
            skLineSegment(sketch, "E65.5.24", {"start": v(19.63, 10.87) * mm, "end": v(22.88, 12.75) * mm});
            skLineSegment(sketch, "E65.5.25", {"start": v(24.96, 12.2) * mm, "end": v(22.88, 12.75) * mm});
            skLineSegment(sketch, "E65.5.26", {"start": v(25.45, 12.48) * mm, "end": v(24.96, 12.2) * mm});
            skLineSegment(sketch, "E65.5.27", {"start": v(25.16, 12.97) * mm, "end": v(25.45, 12.48) * mm});
            skLineSegment(sketch, "E65.5.28", {"start": v(23.86, 13.32) * mm, "end": v(25.16, 12.97) * mm});
            skLineSegment(sketch, "E65.5.29", {"start": v(23.86, 13.32) * mm, "end": v(25.83, 14.45) * mm});
            skLineSegment(sketch, "E65.5.30", {"start": v(25.83, 14.45) * mm, "end": v(25.98, 15) * mm});
            skLineSegment(sketch, "E65.5.31", {"start": v(25.43, 15.15) * mm, "end": v(25.98, 15) * mm});
            skLineSegment(sketch, "E65.5.32", {"start": v(23.46, 14) * mm, "end": v(25.43, 15.15) * mm});
            skLineSegment(sketch, "E65.5.33", {"start": v(23.46, 14) * mm, "end": v(23.81, 15.31) * mm});
            skLineSegment(sketch, "E65.5.34", {"start": v(23.81, 15.31) * mm, "end": v(23.53, 15.8) * mm});
            skLineSegment(sketch, "E65.5.35", {"start": v(23.53, 15.8) * mm, "end": v(23.04, 15.52) * mm});
            skLineSegment(sketch, "E65.5.36", {"start": v(23.04, 15.52) * mm, "end": v(22.48, 13.44) * mm});
            skLineSegment(sketch, "E65.5.37", {"start": v(19.23, 11.56) * mm, "end": v(22.48, 13.44) * mm});
            skLineSegment(sketch, "E65.5.38", {"start": v(19.23, 11.56) * mm, "end": v(20.45, 16.13) * mm});
            skLineSegment(sketch, "E65.5.39", {"start": v(20.45, 16.13) * mm, "end": v(20.17, 16.61) * mm});
            skLineSegment(sketch, "E65.5.40", {"start": v(20.17, 16.61) * mm, "end": v(19.68, 16.33) * mm});
            skLineSegment(sketch, "E65.5.41", {"start": v(19.68, 16.33) * mm, "end": v(18.25, 11) * mm});
            skLineSegment(sketch, "E65.5.42", {"start": v(18.25, 11) * mm, "end": v(17, 10.28) * mm});
            skLineSegment(sketch, "E65.5.43", {"start": v(17, 10.28) * mm, "end": v(14.89, 10.85) * mm});
            skLineSegment(sketch, "E65.5.44", {"start": v(14.89, 10.85) * mm, "end": v(15.93, 14.81) * mm});
            skLineSegment(sketch, "E65.5.45", {"start": v(17.75, 15.87) * mm, "end": v(15.93, 14.81) * mm});
            skLineSegment(sketch, "E65.5.46", {"start": v(17.9, 16.41) * mm, "end": v(17.75, 15.87) * mm});
            skLineSegment(sketch, "E65.5.47", {"start": v(17.35, 16.56) * mm, "end": v(17.9, 16.41) * mm});
            skLineSegment(sketch, "E65.5.48", {"start": v(16.21, 15.9) * mm, "end": v(17.35, 16.56) * mm});
            skLineSegment(sketch, "E65.5.49", {"start": v(16.21, 15.9) * mm, "end": v(17.54, 20.95) * mm});
            skLineSegment(sketch, "E65.5.50", {"start": v(17.54, 20.95) * mm, "end": v(17.26, 21.44) * mm});
            skLineSegment(sketch, "E65.5.51", {"start": v(17.26, 21.44) * mm, "end": v(16.77, 21.16) * mm});
            skLineSegment(sketch, "E65.5.52", {"start": v(16.77, 21.16) * mm, "end": v(15.44, 16.12) * mm});
            skLineSegment(sketch, "E65.5.53", {"start": v(15.44, 16.12) * mm, "end": v(14.8, 17.25) * mm});
            skLineSegment(sketch, "E65.5.54", {"start": v(14.8, 17.25) * mm, "end": v(14.25, 17.4) * mm});
            skLineSegment(sketch, "E65.5.55", {"start": v(14.1, 16.84) * mm, "end": v(14.25, 17.4) * mm});
            skLineSegment(sketch, "E65.5.56", {"start": v(15.15, 15.02) * mm, "end": v(14.1, 16.84) * mm});
            skLineSegment(sketch, "E65.5.57", {"start": v(15.15, 15.02) * mm, "end": v(14.11, 11.06) * mm});
            skLineSegment(sketch, "E65.5.58", {"start": v(14.11, 11.06) * mm, "end": v(12, 11.62) * mm});
            skLineSegment(sketch, "E65.5.59", {"start": v(12, 11.62) * mm, "end": v(9.35, 16.2) * mm});
            skLineSegment(sketch, "E65.5.60", {"start": v(8.66, 15) * mm, "end": v(11.2, 10.6) * mm});
            skLineSegment(sketch, "E65.5.61", {"start": v(11.2, 10.6) * mm, "end": v(16.08, 9.29) * mm});
            skPoint(sketch, "E65.center", {"position": v(0, 0) * mm});
            skPoint(sketch, "E66", {"position": v(-13.64, 9.94) * mm});
            skPoint(sketch, "E67", {"position": v(-13.64, -9.94) * mm});
            skPoint(sketch, "E68", {"position": v(13.64, -9.94) * mm});
            skPoint(sketch, "E69", {"position": v(13.64, 9.94) * mm});
            skLineSegment(sketch, "E70", {"start": v(-13.64, 9.94) * mm, "end": v(13.64, 9.94) * mm, "construction": true});
            skLineSegment(sketch, "E71", {"start": v(13.64, -9.94) * mm, "end": v(13.64, 9.94) * mm, "construction": true});
            skLineSegment(sketch, "E72", {"start": v(13.64, -9.94) * mm, "end": v(-13.64, -9.94) * mm, "construction": true});
            skLineSegment(sketch, "E73", {"start": v(-13.64, 9.94) * mm, "end": v(-13.64, -9.94) * mm, "construction": true});
            skText(sketch, "E74", { "text": "SOFIA", "fontName": "OpenSans-Regular.ttf"});
            skPoint(sketch, "E75", {"position": v(13.64, 0) * mm});
            skCircle(sketch, "E76", {"center": v(0, 31.52) * mm, "radius": 1.16 * mm});
            skCircle(sketch, "E77", {"center": v(0, 31.52) * mm, "radius": 1.96 * mm});
            const initialGuessF0  = {"E74": [-0.01364, -0.00348, 1, 0, 0.00697]};
            skSetInitialGuess(sketch, initialGuessF0);
            skSolve(sketch);
        }
        {
            var Q0;
            Q0=makeQuery(id+"F0.imprint","IMPRINT",FACE,{"disambiguationData":[TD([[makeQuery(id+"F0.imprint","IMPRINT",EDGE,{"derivedFrom":sQuery(id+"F0.wireOp",EDGE,"E3")}),-1.0]])]});
            var sketch = newSketch(context, id + "F1", { "sketchPlane" : qUnion([Q0])});
            skLineSegment(sketch, "E78.0", {"start": v(-13.64, -3.48) * mm, "end": v(13.64, -3.48) * mm, "construction": true});
            skLineSegment(sketch, "E78.1", {"start": v(-17.32, 0) * mm, "end": v(-14.78, -4.4) * mm, "construction": true});
            skLineSegment(sketch, "E79", {"start": v(-15.3, -3.48) * mm, "end": v(15.24, -3.48) * mm, "construction": true});
            skLineSegment(sketch, "E80", {"start": v(15.54, -3.08) * mm, "end": v(-15.54, -3.08) * mm});
            skLineSegment(sketch, "E81.0", {"start": v(-17.32, 0) * mm, "end": v(-15.54, 3.08) * mm, "construction": true});
            skLineSegment(sketch, "E81.1", {"start": v(-13.64, 3.48) * mm, "end": v(13.64, 3.48) * mm, "construction": true});
            skLineSegment(sketch, "E81.2", {"start": v(17.32, 0) * mm, "end": v(14.78, 4.4) * mm, "construction": true});
            skLineSegment(sketch, "E82", {"start": v(-15.3, 3.48) * mm, "end": v(15.3, 3.48) * mm, "construction": true});
            skLineSegment(sketch, "E83", {"start": v(15.3, 3.48) * mm, "end": v(15.54, 3.08) * mm, "construction": true});
            skLineSegment(sketch, "E84", {"start": v(15.54, 3.08) * mm, "end": v(-15.54, 3.08) * mm});
            skLineSegment(sketch, "E85", {"start": v(-15.54, 3.08) * mm, "end": v(-15.3, 3.48) * mm, "construction": true});
            skLineSegment(sketch, "E86", {"start": v(-18.32, 0) * mm, "end": v(-16.3, -3.48) * mm});
            skLineSegment(sketch, "E87", {"start": v(-15.36, 3.4) * mm, "end": v(-15.54, 3.08) * mm});
            skLineSegment(sketch, "E88", {"start": v(-15.54, -3.08) * mm, "end": v(-17.32, 0) * mm});
            skLineSegment(sketch, "E89.trimOffspring", {"start": v(-15.3, 3.48) * mm, "end": v(-14.78, 4.4) * mm, "construction": true});
            skLineSegment(sketch, "E90", {"start": v(18.32, 0) * mm, "end": v(16.54, -3.08) * mm});
            skLineSegment(sketch, "E91", {"start": v(15.54, 3.08) * mm, "end": v(16, 2.28) * mm});
            skLineSegment(sketch, "E92", {"start": v(-15.54, 3.08) * mm, "end": v(-16.54, 3.08) * mm});
            skLineSegment(sketch, "E93", {"start": v(15.54, 3.08) * mm, "end": v(15.54, 3.08) * mm});
            skLineSegment(sketch, "E94", {"start": v(16, 2.28) * mm, "end": v(-16, 2.28) * mm});
            skLineSegment(sketch, "E95", {"start": v(-16.54, 3.08) * mm, "end": v(-18.32, 0) * mm});
            skLineSegment(sketch, "E96", {"start": v(-16, 2.28) * mm, "end": v(-17.32, 0) * mm});
            skLineSegment(sketch, "E97", {"start": v(-15.36, 3.4) * mm, "end": v(-16, 2.28) * mm});
            skLineSegment(sketch, "E98", {"start": v(-16, -2.28) * mm, "end": v(16, -2.28) * mm});
            skLineSegment(sketch, "E99", {"start": v(-15.54, -3.08) * mm, "end": v(-16.54, -3.08) * mm});
            skLineSegment(sketch, "E100", {"start": v(15.54, -3.08) * mm, "end": v(16.54, -3.08) * mm});
            skLineSegment(sketch, "E101", {"start": v(16, -2.28) * mm, "end": v(17.32, 0) * mm});
            skLineSegment(sketch, "E102", {"start": v(16.54, 3.08) * mm, "end": v(18.32, 0) * mm});
            skLineSegment(sketch, "E103", {"start": v(-16.54, -3.08) * mm, "end": v(-16.54, -3.08) * mm});
            skLineSegment(sketch, "E104", {"start": v(16, 2.28) * mm, "end": v(17.32, 0) * mm});
            skLineSegment(sketch, "E105", {"start": v(15.54, 3.08) * mm, "end": v(16.54, 3.08) * mm});
            skSolve(sketch);
        }
        {
            var Q0;
            Q0 = qSketchRegion(id + "F0", true);
            extrude(context, id + "F2", {"entities" : qUnion([Q0]), "depth" : 3 * mm, "offsetDistance" : 25 * mm});
        }
        {
            var Q0;
            Q0 = qSketchRegion(id + "F1", true);
            extrude(context, id + "F3", {"entities" : qUnion([Q0]), "operationType" : NewBodyOperationType.ADD, "depth" : 1.5 * mm, "offsetDistance" : 25 * mm});
        }
        {
            var Q0;
            Q0=makeQuery(id+"F0.imprint","IMPRINT",FACE,{"disambiguationData":[TD([[makeQuery(id+"F0.imprint","IMPRINT",EDGE,{"derivedFrom":sQuery(id+"F0.wireOp",EDGE,"E74.sketch_text.stroke-0")}),-1.0]])]});
            var Q1;
            Q1=makeQuery(id+"F0.imprint","IMPRINT",FACE,{"disambiguationData":[TD([[makeQuery(id+"F0.imprint","IMPRINT",EDGE,{"derivedFrom":sQuery(id+"F0.wireOp",EDGE,"E74.sketch_text.stroke-28")}),-1.0]])]});
            var Q2;
            Q2=makeQuery(id+"F0.imprint","IMPRINT",FACE,{"disambiguationData":[TD([[makeQuery(id+"F0.imprint","IMPRINT",EDGE,{"derivedFrom":sQuery(id+"F0.wireOp",EDGE,"E74.sketch_text.stroke-42")}),-1.0]])]});
            var Q3;
            Q3=makeQuery(id+"F0.imprint","IMPRINT",FACE,{"disambiguationData":[TD([[makeQuery(id+"F0.imprint","IMPRINT",EDGE,{"derivedFrom":sQuery(id+"F0.wireOp",EDGE,"E74.sketch_text.stroke-52")}),-1.0]])]});
            var Q4;
            Q4=makeQuery(id+"F0.imprint","IMPRINT",FACE,{"disambiguationData":[TD([[makeQuery(id+"F0.imprint","IMPRINT",EDGE,{"derivedFrom":sQuery(id+"F0.wireOp",EDGE,"E74.sketch_text.stroke-56")}),-1.0]])]});
            var Q5;
            Q5=makeQuery(id+"F0.imprint","IMPRINT",FACE,{"disambiguationData":[TD([[makeQuery(id+"F0.imprint","IMPRINT",EDGE,{"derivedFrom":sQuery(id+"F0.wireOp",EDGE,"E74.sketch_text.stroke-29")}),-1.0]])]});
            var Q6;
            Q6=makeQuery(id+"F0.imprint","IMPRINT",FACE,{"disambiguationData":[TD([[makeQuery(id+"F0.imprint","IMPRINT",EDGE,{"derivedFrom":sQuery(id+"F0.wireOp",EDGE,"E74.sketch_text.stroke-31")}),-1.0]])]});
            var Q7;
            Q7=makeQuery(id+"F0.imprint","IMPRINT",FACE,{"disambiguationData":[TD([[makeQuery(id+"F0.imprint","IMPRINT",EDGE,{"derivedFrom":sQuery(id+"F0.wireOp",EDGE,"E74.sketch_text.stroke-6")}),-1.0]])]});
            var Q8;
            Q8=makeQuery(id+"F0.imprint","IMPRINT",FACE,{"disambiguationData":[TD([[makeQuery(id+"F0.imprint","IMPRINT",EDGE,{"derivedFrom":sQuery(id+"F0.wireOp",EDGE,"E74.sketch_text.stroke-22")}),-1.0]])]});
            var Q9;
            Q9=makeQuery(id+"F0.imprint","IMPRINT",FACE,{"disambiguationData":[TD([[makeQuery(id+"F0.imprint","IMPRINT",EDGE,{"derivedFrom":sQuery(id+"F0.wireOp",EDGE,"E74.sketch_text.stroke-18")}),-1.0]])]});
            var Q10;
            Q10=makeQuery(id+"F0.imprint","IMPRINT",FACE,{"disambiguationData":[TD([[makeQuery(id+"F0.imprint","IMPRINT",EDGE,{"derivedFrom":sQuery(id+"F0.wireOp",EDGE,"E74.sketch_text.stroke-12")}),-1.0]])]});
            var Q11;
            Q11=makeQuery(id+"F0.imprint","IMPRINT",FACE,{"disambiguationData":[TD([[makeQuery(id+"F0.imprint","IMPRINT",EDGE,{"derivedFrom":sQuery(id+"F0.wireOp",EDGE,"E74.sketch_text.stroke-43")}),-1.0]])]});
            extrude(context, id + "F4", {"entities" : qUnion([Q0, Q1, Q2, Q3, Q4, Q5, Q6, Q7, Q8, Q9, Q10, Q11]), "operationType" : NewBodyOperationType.ADD, "depth" : 3 * mm, "offsetDistance" : 25 * mm});
        }
        {
            var Q0;
            Q0=makeQuery(id+"F3.boolean.opBoolean","INTERSECT",EDGE,{"derivedFrom":[makeQuery(id+"F2.opExtrude","SWEPT_FACE",FACE,{"disambiguationData":[OSD([sQuery(id+"F0.wireOp",EDGE,"E65.1.60")])]}),makeQuery(id+"F3.opExtrude","CAP_FACE",FACE,{"disambiguationData":[OSD([sQuery(id+"F1.wireOp",EDGE,"E79"),sQuery(id+"F1.wireOp",EDGE,"E80"),sQuery(id+"F1.wireOp",EDGE,"E82"),sQuery(id+"F1.wireOp",EDGE,"E84"),sQuery(id+"F1.wireOp",EDGE,"XHNybsxl-Ojz6-RINM-ekfA-wkJ97r4N2FFI"),sQuery(id+"F1.wireOp",EDGE,"gJpL6BSq-HIsu-dALy-FR7s-Pzfzj7Ko7oFS"),sQuery(id+"F1.wireOp",EDGE,"E86"),sQuery(id+"F1.wireOp",EDGE,"zG8Sn3pr-TeTJ-NiNP-bkra-72UvK1kdMZe8"),sQuery(id+"F1.wireOp",EDGE,"E87"),sQuery(id+"F1.wireOp",EDGE,"E88"),sQuery(id+"F1.wireOp",EDGE,"KcmRWpFm-FUaA-xYRB-SBfS-EbFkVParo1UT"),sQuery(id+"F1.wireOp",EDGE,"IXizUj2u-6gyy-uYQN-PQwd-BXqFSfkT0ZYb"),sQuery(id+"F1.wireOp",EDGE,"E90"),sQuery(id+"F1.wireOp",EDGE,"L0DsdSoC-T2fO-xfwq-GFRs-WkKR04X5DteX"),sQuery(id+"F1.wireOp",EDGE,"5B30pRPh-UxHn-CQqJ-FdMT-PAFcgRZIHgIV"),sQuery(id+"F1.wireOp",EDGE,"E91")])],"isStart":false})]});
            var Q1;
            Q1=makeQuery(id+"F3.boolean.opBoolean","INTERSECT",EDGE,{"derivedFrom":[makeQuery(id+"F2.opExtrude","SWEPT_FACE",FACE,{"disambiguationData":[OSD([sQuery(id+"F0.wireOp",EDGE,"E65.2.1")])]}),makeQuery(id+"F3.opExtrude","CAP_FACE",FACE,{"disambiguationData":[OSD([sQuery(id+"F1.wireOp",EDGE,"E79"),sQuery(id+"F1.wireOp",EDGE,"E80"),sQuery(id+"F1.wireOp",EDGE,"E82"),sQuery(id+"F1.wireOp",EDGE,"E84"),sQuery(id+"F1.wireOp",EDGE,"XHNybsxl-Ojz6-RINM-ekfA-wkJ97r4N2FFI"),sQuery(id+"F1.wireOp",EDGE,"gJpL6BSq-HIsu-dALy-FR7s-Pzfzj7Ko7oFS"),sQuery(id+"F1.wireOp",EDGE,"E86"),sQuery(id+"F1.wireOp",EDGE,"zG8Sn3pr-TeTJ-NiNP-bkra-72UvK1kdMZe8"),sQuery(id+"F1.wireOp",EDGE,"E87"),sQuery(id+"F1.wireOp",EDGE,"E88"),sQuery(id+"F1.wireOp",EDGE,"KcmRWpFm-FUaA-xYRB-SBfS-EbFkVParo1UT"),sQuery(id+"F1.wireOp",EDGE,"IXizUj2u-6gyy-uYQN-PQwd-BXqFSfkT0ZYb"),sQuery(id+"F1.wireOp",EDGE,"E90"),sQuery(id+"F1.wireOp",EDGE,"L0DsdSoC-T2fO-xfwq-GFRs-WkKR04X5DteX"),sQuery(id+"F1.wireOp",EDGE,"5B30pRPh-UxHn-CQqJ-FdMT-PAFcgRZIHgIV"),sQuery(id+"F1.wireOp",EDGE,"E91")])],"isStart":false})]});
            var Q2;
            Q2=makeQuery(id+"F3.boolean.opBoolean","INTERSECT",EDGE,{"derivedFrom":[makeQuery(id+"F2.opExtrude","SWEPT_FACE",FACE,{"disambiguationData":[OSD([sQuery(id+"F0.wireOp",EDGE,"E65.5.1")])]}),makeQuery(id+"F3.opExtrude","CAP_FACE",FACE,{"disambiguationData":[OSD([sQuery(id+"F1.wireOp",EDGE,"E79"),sQuery(id+"F1.wireOp",EDGE,"E80"),sQuery(id+"F1.wireOp",EDGE,"E82"),sQuery(id+"F1.wireOp",EDGE,"E84"),sQuery(id+"F1.wireOp",EDGE,"XHNybsxl-Ojz6-RINM-ekfA-wkJ97r4N2FFI"),sQuery(id+"F1.wireOp",EDGE,"gJpL6BSq-HIsu-dALy-FR7s-Pzfzj7Ko7oFS"),sQuery(id+"F1.wireOp",EDGE,"E86"),sQuery(id+"F1.wireOp",EDGE,"zG8Sn3pr-TeTJ-NiNP-bkra-72UvK1kdMZe8"),sQuery(id+"F1.wireOp",EDGE,"E87"),sQuery(id+"F1.wireOp",EDGE,"E88"),sQuery(id+"F1.wireOp",EDGE,"KcmRWpFm-FUaA-xYRB-SBfS-EbFkVParo1UT"),sQuery(id+"F1.wireOp",EDGE,"IXizUj2u-6gyy-uYQN-PQwd-BXqFSfkT0ZYb"),sQuery(id+"F1.wireOp",EDGE,"E90"),sQuery(id+"F1.wireOp",EDGE,"L0DsdSoC-T2fO-xfwq-GFRs-WkKR04X5DteX"),sQuery(id+"F1.wireOp",EDGE,"5B30pRPh-UxHn-CQqJ-FdMT-PAFcgRZIHgIV"),sQuery(id+"F1.wireOp",EDGE,"E91")])],"isStart":false})]});
            var Q3;
            Q3=makeQuery(id+"F3.boolean.opBoolean","INTERSECT",EDGE,{"derivedFrom":[makeQuery(id+"F2.opExtrude","SWEPT_FACE",FACE,{"disambiguationData":[OSD([sQuery(id+"F0.wireOp",EDGE,"E65.4.60")])]}),makeQuery(id+"F3.opExtrude","CAP_FACE",FACE,{"disambiguationData":[OSD([sQuery(id+"F1.wireOp",EDGE,"E79"),sQuery(id+"F1.wireOp",EDGE,"E80"),sQuery(id+"F1.wireOp",EDGE,"E82"),sQuery(id+"F1.wireOp",EDGE,"E84"),sQuery(id+"F1.wireOp",EDGE,"XHNybsxl-Ojz6-RINM-ekfA-wkJ97r4N2FFI"),sQuery(id+"F1.wireOp",EDGE,"gJpL6BSq-HIsu-dALy-FR7s-Pzfzj7Ko7oFS"),sQuery(id+"F1.wireOp",EDGE,"E86"),sQuery(id+"F1.wireOp",EDGE,"zG8Sn3pr-TeTJ-NiNP-bkra-72UvK1kdMZe8"),sQuery(id+"F1.wireOp",EDGE,"E87"),sQuery(id+"F1.wireOp",EDGE,"E88"),sQuery(id+"F1.wireOp",EDGE,"KcmRWpFm-FUaA-xYRB-SBfS-EbFkVParo1UT"),sQuery(id+"F1.wireOp",EDGE,"IXizUj2u-6gyy-uYQN-PQwd-BXqFSfkT0ZYb"),sQuery(id+"F1.wireOp",EDGE,"E90"),sQuery(id+"F1.wireOp",EDGE,"L0DsdSoC-T2fO-xfwq-GFRs-WkKR04X5DteX"),sQuery(id+"F1.wireOp",EDGE,"5B30pRPh-UxHn-CQqJ-FdMT-PAFcgRZIHgIV"),sQuery(id+"F1.wireOp",EDGE,"E91")])],"isStart":false})]});
            chamfer(context, id + "F5", {"entities" : qUnion([Q0, Q1, Q2, Q3]), "width" : 1.2 * mm, "tangentPropagation" : true});
        }
    });
